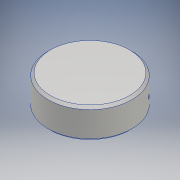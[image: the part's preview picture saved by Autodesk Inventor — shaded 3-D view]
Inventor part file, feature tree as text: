
AUTODESK INVENTOR PART (.ipt)
format: ipt  version: 2017 (Build 210142000, 142)  size: 146,944 bytes
history: native  units: mm
features: sketch x6, plane x4, hole x4, thread x4, extrude x1, chamfer x1
ambient origin geometry x8: Origin, YZ Plane, XZ Plane, XY Plane, X Axis, Y Axis, Z Axis, Center Point
bodies: Solid1 (feature_tree)
feature tree (20):
  extrude  "Extrusion1"  Depth=25.0mm TaperAngle=0.0deg
  chamfer  "Chamfer1"  Distance=2.0mm Angle=45.0deg
  sketch  "Sketch2"  dims[d6=6.684611mm d7=9.986774mm]
  plane  "Work Plane1"
  plane  "Work Plane2"
  plane  "Work Plane3"
  plane  "Work Plane4"
  sketch  "Sketch3"  dims[d8=14.5mm d9=14.5mm]
  sketch  "Sketch4"  dims[d10=14.5mm d11=14.5mm]
  sketch  "Sketch5"  dims[d12=3.0mm d13=6.0mm d14=4.0mm d15=2.0mm d16=90.0deg d17=8.0mm d18=20.594885mm]
  hole  "Hole1"  [1 undecoded]
  hole  "Hole2"  [1 undecoded]
  hole  "Hole3"  [1 undecoded]
  hole  "Hole4"  [1 undecoded]
  thread  "Thread1"  [1 undecoded]
  thread  "Thread2"  [1 undecoded]
  thread  "Thread3"  [1 undecoded]
  thread  "Thread4"  [1 undecoded]
  sketch  "Sketch1"  dims[d0=70.0mm d1=25.0mm d2=0.0mm d3=2.0mm d4=2.0mm d5=45.0deg]
  sketch  "Sketch6"  dims[d19=3.0mm d20=6.0mm d21=4.0mm d22=2.0mm d23=90.0deg d24=8.0mm d25=20.594885mm d26=3.0mm d27=6.0mm d28=4.0mm d29=2.0mm d30=90.0deg d31=8.0mm d32=20.594885mm d33=3.0mm d34=6.0mm d35=4.0mm d36=2.0mm d37=90.0deg d38=8.0mm d39=20.594885mm d40=10.0mm d41=0.0mm d42=10.0mm d43=0.0mm d44=10.0mm d45=0.0mm d46=10.0mm d47=0.0mm]
note: 8 required parameter values undecoded (feature->parameter linkage not recoverable at this tier; creation-order binding heuristic only, values carry confidence <= 0.55)
